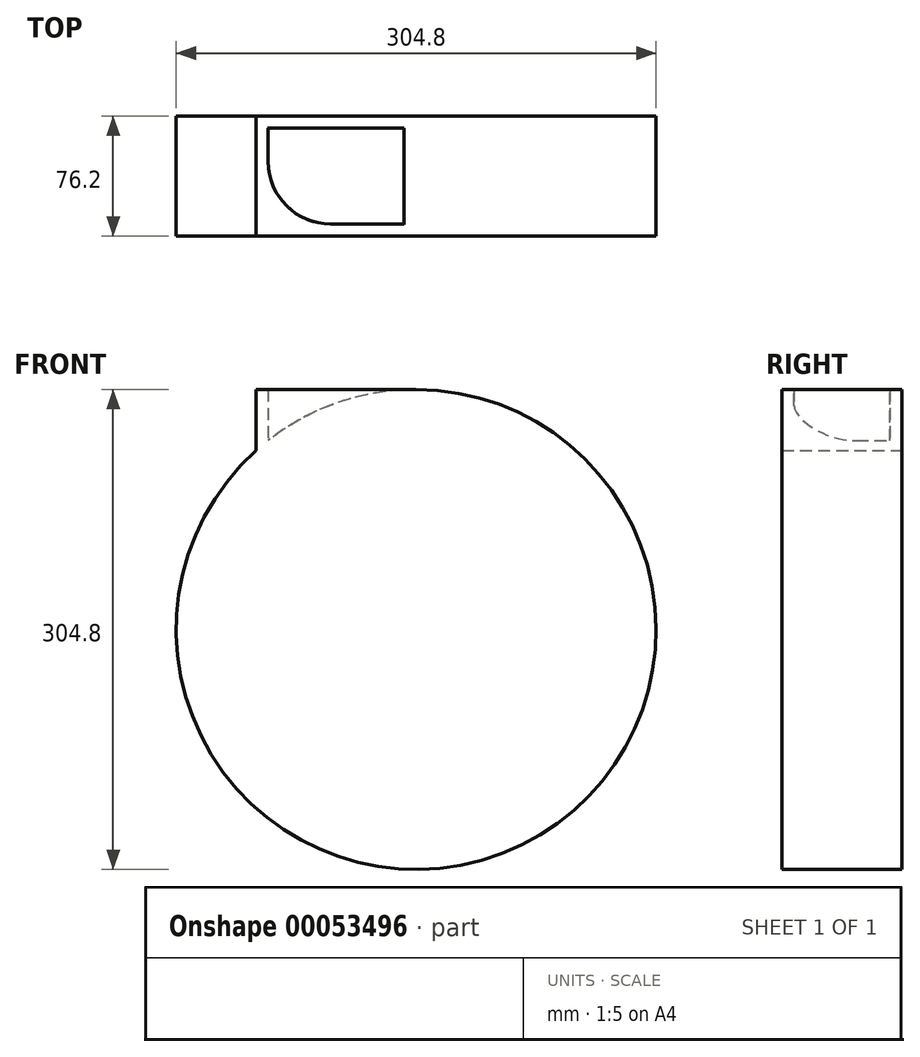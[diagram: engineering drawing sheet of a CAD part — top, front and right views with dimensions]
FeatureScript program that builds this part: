
annotation { "Feature Type Name" : "Feature", "Feature Type Description" : "" }
export const myFeature = defineFeature(function(context is Context, id is Id, definition is map)
    precondition{}
    {
        {
            var Q0;
            Q0=qCreatedBy(makeId("Top.planeOp"),FACE);
            var sketch = newSketch(context, id + "F0", { "sketchPlane" : qUnion([Q0])});
            skLineSegment(sketch, "E0.bottom", {"start": v(-57.14, 51.94) * mm, "end": v(44.46, 51.94) * mm});
            skLineSegment(sketch, "E0.top", {"start": v(-57.14, -24.26) * mm, "end": v(44.46, -24.26) * mm});
            skLineSegment(sketch, "E0.left", {"start": v(-57.14, 51.94) * mm, "end": v(-57.14, -24.26) * mm});
            skLineSegment(sketch, "E0.right", {"start": v(44.46, 51.94) * mm, "end": v(44.46, -24.26) * mm});
            skSolve(sketch);
        }
        {
            var Q0;
            Q0=makeQuery(id+"F0.imprint","IMPRINT",FACE,{"disambiguationData":[TD([[makeQuery(id+"F0.imprint","IMPRINT",EDGE,{"derivedFrom":sQuery(id+"F0.wireOp",EDGE,"E0.bottom")}),-1.0]])]});
            extrude(context, id + "F1", {"entities" : qUnion([Q0]), "depth" : 152.4 * mm});
        }
        {
            var Q0;
            Q0=makeQuery(id+"F1.opExtrude","CAP_FACE",FACE,{"disambiguationData":[OSD([sQuery(id+"F0.wireOp",EDGE,"E0.bottom"),sQuery(id+"F0.wireOp",EDGE,"E0.top"),sQuery(id+"F0.wireOp",EDGE,"E0.left"),sQuery(id+"F0.wireOp",EDGE,"E0.right")])],"isStart":false});
            shell(context, id + "F2", {"entities" : qUnion([Q0]), "thickness" : 7.62 * mm});
        }
        {
            var Q0;
            Q0=makeQuery(id+"F2.opShell","OFFSET_EDGE",EDGE,{"disambiguationData":[OSD([sQuery(id+"F0.wireOp",EDGE,"E0.top"),sQuery(id+"F0.wireOp",EDGE,"E0.left")])]});
            fillet(context, id + "F3", {"entities" : qUnion([Q0]), "radius" : 39.7 * mm, "tangentPropagation" : true, "allowEdgeOverflow" : false});
        }
        {
            var Q0;
            Q0=makeQuery(id+"F1.opExtrude","SWEPT_FACE",FACE,{"disambiguationData":[OSD([sQuery(id+"F0.wireOp",EDGE,"E0.right")])]});
            var Q1;
            Q1=makeQuery(id+"F1.opExtrude","CAP_EDGE",EDGE,{"disambiguationData":[OSD([sQuery(id+"F0.wireOp",EDGE,"E0.right")])],"isStart":true});
            revolve(context, id + "F4", {"operationType" : NewBodyOperationType.ADD, "entities" : qUnion([Q0]), "axis" : qUnion([Q1]), "revolveType" : RevolveType.FULL});
        }
        {
            var Q0;
            {var subQ0=sQuery(id+"F0.wireOp",EDGE,"E0.left");var subQ1=sQuery(id+"F0.wireOp",EDGE,"E0.top");Q0=makeQuery(id+"F3.opFillet","BLEND_EDGE",EDGE,{"blendedFrom":[makeQuery(id+"F2.opShell","OFFSET_EDGE",EDGE,{"disambiguationData":[OSD([subQ1,subQ0])]}),makeQuery(id+"F1.opExtrude","CAP_FACE",FACE,{"disambiguationData":[OSD([sQuery(id+"F0.wireOp",EDGE,"E0.bottom"),subQ1,subQ0,sQuery(id+"F0.wireOp",EDGE,"E0.right")])],"isStart":false})],"blendedInto":[makeQuery(id+"F1.opExtrude","CAP_FACE",FACE,{"disambiguationData":[OSD([sQuery(id+"F0.wireOp",EDGE,"E0.bottom"),subQ1,subQ0,sQuery(id+"F0.wireOp",EDGE,"E0.right")])],"isStart":false})]});}
            fillet(context, id + "F5", {"entities" : qUnion([Q0]), "radius" : 0.24 * mm, "tangentPropagation" : true, "allowEdgeOverflow" : false});
        }
    });
